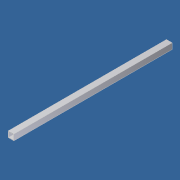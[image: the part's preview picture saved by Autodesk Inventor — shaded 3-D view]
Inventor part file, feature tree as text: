
AUTODESK INVENTOR PART (.ipt)
format: ipt  version: 2012 (Build 160160000, 160)  size: 72,192 bytes
history: native  units: in
note: dims shown in document units (in); Inventor stores cm internally (conversion verified against a paired STEP export)
features: extrude x1, sketch x1
ambient origin geometry x8: Origin, YZ Plane, XZ Plane, XY Plane, X Axis, Y Axis, Z Axis, Center Point
bodies: Solid1 (feature_tree)
feature tree (2):
  extrude  "Extrusion1"  Depth=1.75in
  sketch  "Sketch1"  dims[d0=1.75in d1=1.75in d2=0.125in d3=48.0in d4=0.0in]
